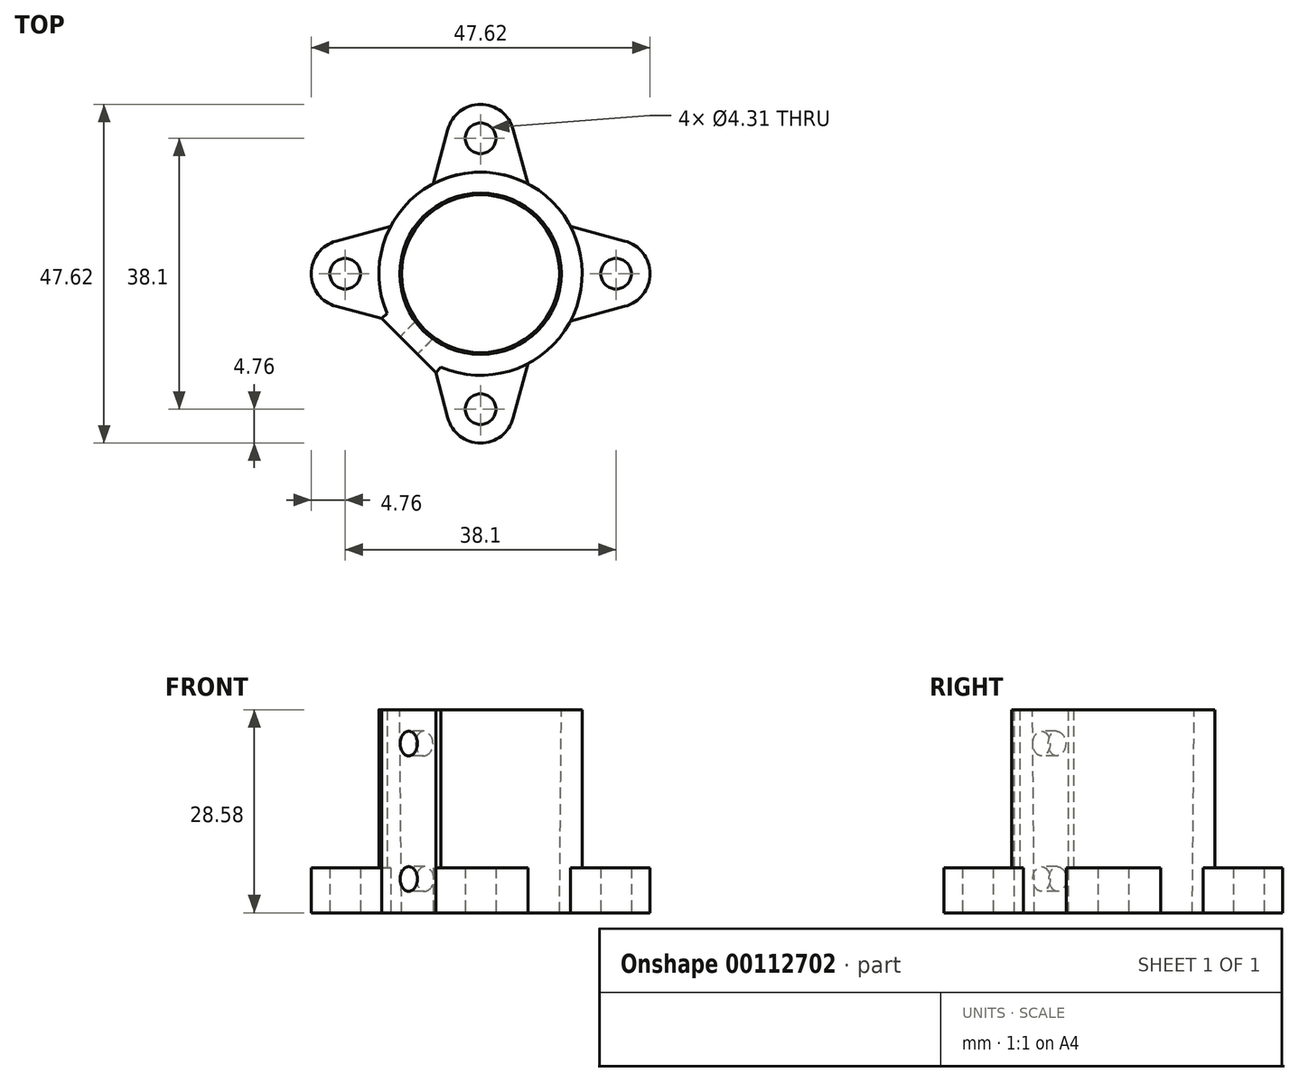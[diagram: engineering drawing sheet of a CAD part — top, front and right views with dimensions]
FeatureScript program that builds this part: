
annotation { "Feature Type Name" : "Feature", "Feature Type Description" : "" }
export const myFeature = defineFeature(function(context is Context, id is Id, definition is map)
    precondition{}
    {
        {
            var Q0;
            Q0=qCreatedBy(makeId("Top.planeOp"),FACE);
            var sketch = newSketch(context, id + "F0", { "sketchPlane" : qUnion([Q0])});
            skCircle(sketch, "E0", {"center": v(0, 0) * mm, "radius": 11.11 * mm});
            skLineSegment(sketch, "E1", {"start": v(0, 19.05) * mm, "end": v(0, -19.05) * mm, "construction": true});
            skLineSegment(sketch, "E2", {"start": v(-19.05, 0) * mm, "end": v(19.05, 0) * mm, "construction": true});
            skCircle(sketch, "E3", {"center": v(0, 19.05) * mm, "radius": 2.15 * mm});
            skCircle(sketch, "E4", {"center": v(19.05, 0) * mm, "radius": 2.15 * mm});
            skCircle(sketch, "E5", {"center": v(0, -19.05) * mm, "radius": 2.15 * mm});
            skCircle(sketch, "E6", {"center": v(-19.05, 0) * mm, "radius": 2.15 * mm});
            skArc(sketch, "E7", {"start": v(4.6, 20.28) * mm, "mid": v(0, 23.81) * mm, "end": v(-4.6, 20.28) * mm});
            skLineSegment(sketch, "E8", {"start": v(-4.6, 20.28) * mm, "end": v(-6.65, 12.65) * mm});
            skLineSegment(sketch, "E9", {"start": v(4.6, 20.28) * mm, "end": v(6.65, 12.65) * mm});
            skArc(sketch, "E10", {"start": v(-6.65, 12.65) * mm, "mid": v(-10.1, 10.1) * mm, "end": v(-12.65, 6.65) * mm});
            skLineSegment(sketch, "E11", {"start": v(-4.6, 20.28) * mm, "end": v(4.6, 20.28) * mm, "construction": true});
            skArc(sketch, "E12", {"start": v(20.28, -4.6) * mm, "mid": v(23.81, 0) * mm, "end": v(20.28, 4.6) * mm});
            skArc(sketch, "E13", {"start": v(-4.6, -20.28) * mm, "mid": v(0, -23.81) * mm, "end": v(4.6, -20.28) * mm});
            skArc(sketch, "E14", {"start": v(-20.28, 4.6) * mm, "mid": v(-23.81, 0) * mm, "end": v(-20.28, -4.6) * mm});
            skLineSegment(sketch, "E15", {"start": v(-20.28, 4.6) * mm, "end": v(-12.65, 6.65) * mm});
            skLineSegment(sketch, "E16", {"start": v(-20.28, 4.6) * mm, "end": v(-20.28, -4.6) * mm, "construction": true});
            skLineSegment(sketch, "E17", {"start": v(20.28, -4.6) * mm, "end": v(12.65, -6.65) * mm});
            skLineSegment(sketch, "E18", {"start": v(20.28, 4.6) * mm, "end": v(12.65, 6.65) * mm});
            skLineSegment(sketch, "E19", {"start": v(-20.28, -4.6) * mm, "end": v(-12.65, -6.65) * mm});
            skLineSegment(sketch, "E20", {"start": v(-4.6, -20.28) * mm, "end": v(4.6, -20.28) * mm, "construction": true});
            skLineSegment(sketch, "E21", {"start": v(20.28, -4.6) * mm, "end": v(20.28, 4.6) * mm, "construction": true});
            skLineSegment(sketch, "E22", {"start": v(-4.6, -20.28) * mm, "end": v(-6.65, -12.65) * mm});
            skLineSegment(sketch, "E23", {"start": v(4.6, -20.28) * mm, "end": v(6.65, -12.65) * mm});
            skArc(sketch, "E24", {"start": v(-12.65, -6.65) * mm, "mid": v(-10.1, -10.1) * mm, "end": v(-6.65, -12.65) * mm});
            skArc(sketch, "E25", {"start": v(6.65, -12.65) * mm, "mid": v(10.1, -10.1) * mm, "end": v(12.65, -6.65) * mm});
            skArc(sketch, "E26", {"start": v(12.65, 6.65) * mm, "mid": v(10.1, 10.1) * mm, "end": v(6.65, 12.65) * mm});
            skSolve(sketch);
        }
        {
            var Q0;
            Q0 = qSketchRegion(id + "F0", true);
            extrude(context, id + "F1", {"entities" : qUnion([Q0]), "depth" : 6.35 * mm});
        }
        {
            var Q0;
            Q0=makeQuery(id+"F1.opExtrude","CAP_FACE",FACE,{"disambiguationData":[OSD([sQuery(id+"F0.wireOp",EDGE,"E0"),sQuery(id+"F0.wireOp",EDGE,"E3"),sQuery(id+"F0.wireOp",EDGE,"E4"),sQuery(id+"F0.wireOp",EDGE,"E5"),sQuery(id+"F0.wireOp",EDGE,"E6"),sQuery(id+"F0.wireOp",EDGE,"E7"),sQuery(id+"F0.wireOp",EDGE,"E8"),sQuery(id+"F0.wireOp",EDGE,"E9"),sQuery(id+"F0.wireOp",EDGE,"E10"),sQuery(id+"F0.wireOp",EDGE,"E12"),sQuery(id+"F0.wireOp",EDGE,"E13"),sQuery(id+"F0.wireOp",EDGE,"E14"),sQuery(id+"F0.wireOp",EDGE,"E15"),sQuery(id+"F0.wireOp",EDGE,"E17"),sQuery(id+"F0.wireOp",EDGE,"E18"),sQuery(id+"F0.wireOp",EDGE,"E19"),sQuery(id+"F0.wireOp",EDGE,"E22"),sQuery(id+"F0.wireOp",EDGE,"E23"),sQuery(id+"F0.wireOp",EDGE,"E24"),sQuery(id+"F0.wireOp",EDGE,"E25"),sQuery(id+"F0.wireOp",EDGE,"E26")])],"isStart":false});
            var sketch = newSketch(context, id + "F2", { "sketchPlane" : qUnion([Q0])});
            skCircle(sketch, "E27", {"center": v(0, 0) * mm, "radius": 11.11 * mm});
            skCircle(sketch, "E28", {"center": v(0, 0) * mm, "radius": 14.29 * mm});
            skSolve(sketch);
        }
        {
            var Q0;
            Q0 = qSketchRegion(id + "F2", true);
            extrude(context, id + "F3", {"entities" : qUnion([Q0]), "operationType" : NewBodyOperationType.ADD, "depth" : 22.22 * mm});
        }
        {
            var Q0;
            Q0=makeQuery(id+"F3.opExtrude","CAP_FACE",FACE,{"disambiguationData":[OSD([sQuery(id+"F2.wireOp",EDGE,"E27"),sQuery(id+"F2.wireOp",EDGE,"E28")])],"isStart":false});
            var sketch = newSketch(context, id + "F4", { "sketchPlane" : qUnion([Q0])});
            skLineSegment(sketch, "E29.bottom", {"start": v(-11.65, -4.07) * mm, "end": v(-4.07, -11.65) * mm});
            skLineSegment(sketch, "E29.top", {"start": v(-13.9, -6.31) * mm, "end": v(-6.31, -13.9) * mm});
            skLineSegment(sketch, "E29.left", {"start": v(-11.65, -4.07) * mm, "end": v(-13.9, -6.31) * mm});
            skLineSegment(sketch, "E29.right", {"start": v(-4.07, -11.65) * mm, "end": v(-6.31, -13.9) * mm});
            skLineSegment(sketch, "E30", {"start": v(-7.86, -7.86) * mm, "end": v(0, 0) * mm, "construction": true});
            skLineSegment(sketch, "E31", {"start": v(0, 0) * mm, "end": v(0, -7.86) * mm, "construction": true});
            skLineSegment(sketch, "E32", {"start": v(-7.86, -7.86) * mm, "end": v(0, -7.86) * mm, "construction": true});
            skSolve(sketch);
        }
        {
            var Q0;
            Q0 = qSketchRegion(id + "F4", true);
            var Q1;
            Q1=makeQuery(id+"F1.opExtrude","CAP_FACE",FACE,{"disambiguationData":[OSD([sQuery(id+"F0.wireOp",EDGE,"E0"),sQuery(id+"F0.wireOp",EDGE,"E3"),sQuery(id+"F0.wireOp",EDGE,"E4"),sQuery(id+"F0.wireOp",EDGE,"E5"),sQuery(id+"F0.wireOp",EDGE,"E6"),sQuery(id+"F0.wireOp",EDGE,"E7"),sQuery(id+"F0.wireOp",EDGE,"E8"),sQuery(id+"F0.wireOp",EDGE,"E9"),sQuery(id+"F0.wireOp",EDGE,"E10"),sQuery(id+"F0.wireOp",EDGE,"E12"),sQuery(id+"F0.wireOp",EDGE,"E13"),sQuery(id+"F0.wireOp",EDGE,"E14"),sQuery(id+"F0.wireOp",EDGE,"E15"),sQuery(id+"F0.wireOp",EDGE,"E17"),sQuery(id+"F0.wireOp",EDGE,"E18"),sQuery(id+"F0.wireOp",EDGE,"E19"),sQuery(id+"F0.wireOp",EDGE,"E22"),sQuery(id+"F0.wireOp",EDGE,"E23"),sQuery(id+"F0.wireOp",EDGE,"E24"),sQuery(id+"F0.wireOp",EDGE,"E25"),sQuery(id+"F0.wireOp",EDGE,"E26")])],"isStart":true});
            extrude(context, id + "F5", {"entities" : qUnion([Q0]), "operationType" : NewBodyOperationType.ADD, "endBound" : BoundingType.UP_TO_SURFACE, "oppositeDirection" : true, "endBoundEntityFace" : qUnion([Q1]), "depth" : 25.4 * mm});
        }
        {
            var Q0;
            Q0=makeQuery(id+"F5.opExtrude","SWEPT_FACE",FACE,{"disambiguationData":[OSD([sQuery(id+"F4.wireOp",EDGE,"E29.top")])]});
            var sketch = newSketch(context, id + "F6", { "sketchPlane" : qUnion([Q0])});
            skLineSegment(sketch, "E33", {"start": v(0, 0) * mm, "end": v(0, 4.76) * mm, "construction": true});
            skLineSegment(sketch, "E34", {"start": v(0, 28.58) * mm, "end": v(0, 23.81) * mm, "construction": true});
            skCircle(sketch, "E35", {"center": v(0, 23.81) * mm, "radius": 1.73 * mm});
            skCircle(sketch, "E36", {"center": v(0, 4.76) * mm, "radius": 1.73 * mm});
            skSolve(sketch);
        }
        {
            var Q0;
            Q0 = qSketchRegion(id + "F6", true);
            var Q1;
            Q1=makeQuery(id+"F3.boolean.opBoolean","MERGE",FACE,{"derivedFrom":[makeQuery(id+"F1.opExtrude","SWEPT_FACE",FACE,{"disambiguationData":[OSD([sQuery(id+"F0.wireOp",EDGE,"E0")])]}),makeQuery(id+"F3.opExtrude","SWEPT_FACE",FACE,{"disambiguationData":[OSD([sQuery(id+"F2.wireOp",EDGE,"E27")])]})]});
            extrude(context, id + "F7", {"entities" : qUnion([Q0]), "operationType" : NewBodyOperationType.REMOVE, "endBound" : BoundingType.UP_TO_SURFACE, "oppositeDirection" : true, "endBoundEntityFace" : qUnion([Q1]), "depth" : 25.4 * mm});
        }
        {
            var Q0;
            Q0=makeQuery(id+"F3.opExtrude","CAP_EDGE",EDGE,{"disambiguationData":[OSD([sQuery(id+"F2.wireOp",EDGE,"E27")])],"isStart":false});
            chamfer(context, id + "F8", {"entities" : qUnion([Q0]), "chamferType" : ChamferType.TWO_OFFSETS, "width1" : 28.57 * mm, "oppositeDirection" : false, "width2" : 0.25 * mm, "tangentPropagation" : true});
        }
    });
